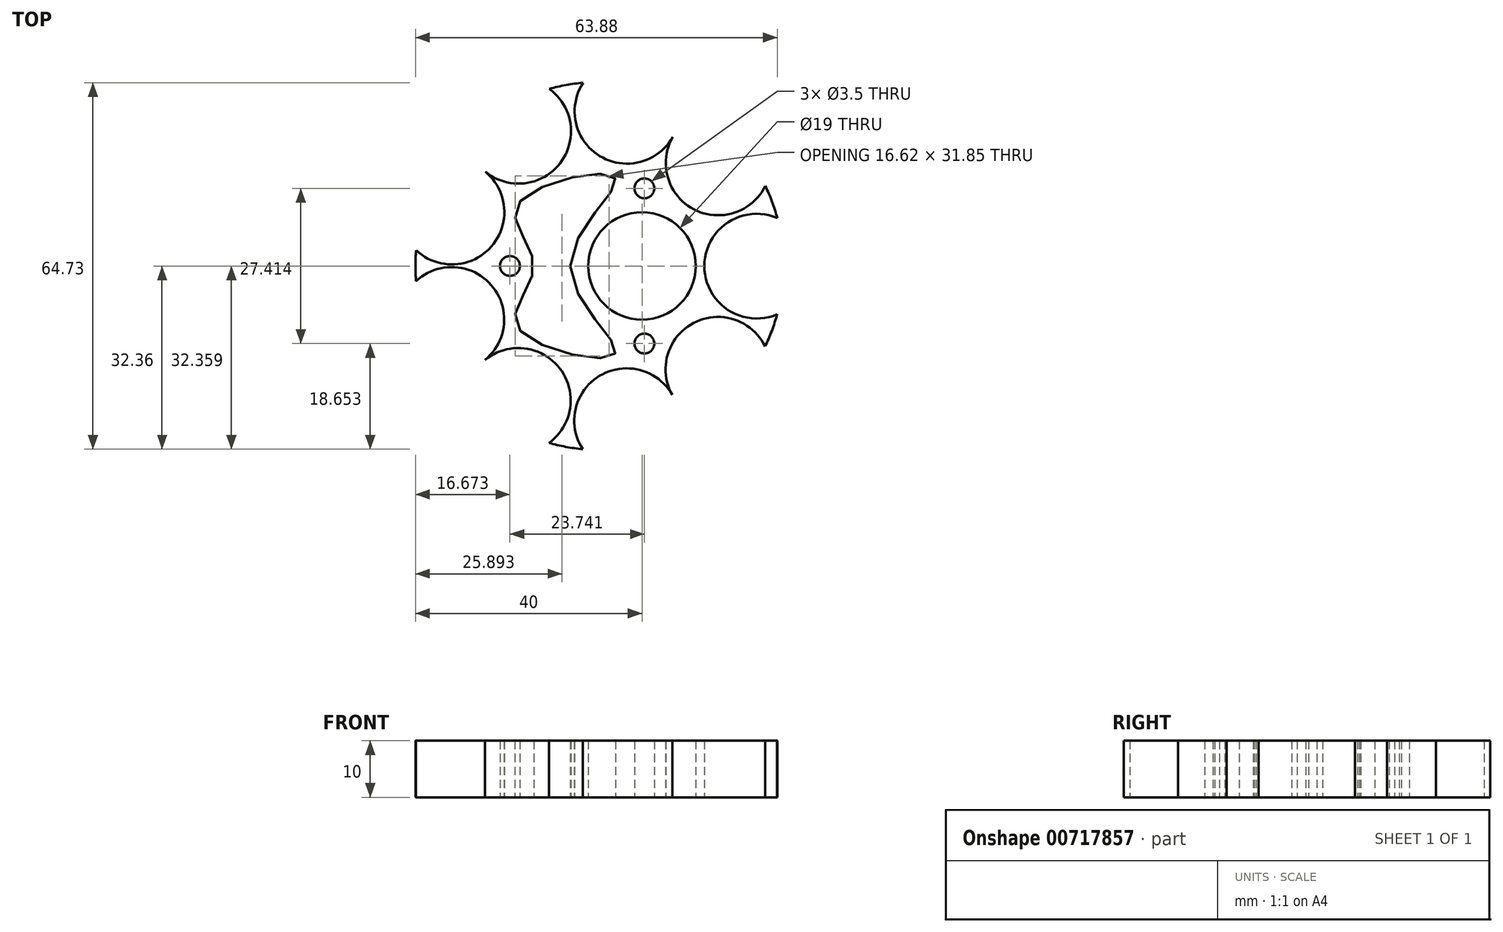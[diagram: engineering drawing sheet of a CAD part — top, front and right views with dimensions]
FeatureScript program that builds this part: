
annotation { "Feature Type Name" : "Feature", "Feature Type Description" : "" }
export const myFeature = defineFeature(function(context is Context, id is Id, definition is map)
    precondition{}
    {
        {
            var Q0;
            Q0=qCreatedBy(makeId("Top.planeOp"),FACE);
            var sketch = newSketch(context, id + "F0", { "sketchPlane" : qUnion([Q0])});
            skCircle(sketch, "E0", {"center": v(0, 0) * mm, "radius": 32.5 * mm});
            skCircle(sketch, "E1", {"center": v(27.75, -0.04) * mm, "radius": 9.25 * mm});
            skCircle(sketch, "E2.1.0", {"center": v(20.95, 18.2) * mm, "radius": 9.25 * mm});
            skCircle(sketch, "E2.2.0", {"center": v(4.85, 27.32) * mm, "radius": 9.25 * mm});
            skCircle(sketch, "E2.3.0", {"center": v(-14.29, 23.8) * mm, "radius": 9.25 * mm});
            skCircle(sketch, "E2.4.0", {"center": v(-26.06, 9.52) * mm, "radius": 9.25 * mm});
            skCircle(sketch, "E2.5.0", {"center": v(-26.09, -9.46) * mm, "radius": 9.25 * mm});
            skCircle(sketch, "E2.6.0", {"center": v(-14.35, -23.75) * mm, "radius": 9.25 * mm});
            skCircle(sketch, "E2.7.0", {"center": v(4.78, -27.33) * mm, "radius": 9.25 * mm});
            skCircle(sketch, "E2.8.0", {"center": v(20.9, -18.25) * mm, "radius": 9.25 * mm});
            skCircle(sketch, "E3", {"center": v(7.5, 0) * mm, "radius": 9.5 * mm});
            skCircle(sketch, "E4", {"center": v(-15.83, 0) * mm, "radius": 1.75 * mm});
            skCircle(sketch, "E5.1.0", {"center": v(7.91, -13.7) * mm, "radius": 1.75 * mm});
            skCircle(sketch, "E5.2.0", {"center": v(7.91, 13.7) * mm, "radius": 1.75 * mm});
            skPoint(sketch, "E6", {"position": v(2.64, 15.6) * mm});
            skPoint(sketch, "E7.MirrorP", {"position": v(2.64, -15.6) * mm});
            skPoint(sketch, "E8", {"position": v(-5.2, 0) * mm});
            skPoint(sketch, "E9", {"position": v(-11.6, 0) * mm});
            skPoint(sketch, "E10", {"position": v(-14.5, 10.8) * mm});
            skPoint(sketch, "E11.MirrorP", {"position": v(-14.5, -10.8) * mm});
            skFitSpline(sketch, "E12", {"points": [v(-5.2, 0) * mm, v(2.64, 15.6) * mm, v(-14.5, 10.8) * mm, v(-11.6, 0) * mm, v(-14.5, -10.8) * mm, v(2.64, -15.6) * mm, v(-5.2, 0) * mm]});
            skCircle(sketch, "E13", {"center": v(0, 0) * mm, "radius": 37 * mm, "construction": true});
            skSolve(sketch);
        }
        {
            var Q0;
            Q0=makeQuery(id+"F0.imprint","IMPRINT",FACE,{"disambiguationData":[TD([[makeQuery(id+"F0.imprint","IMPRINT",EDGE,{"derivedFrom":sQuery(id+"F0.wireOp",EDGE,"E4")}),-1.0]])]});
            extrude(context, id + "F1", {"entities" : qUnion([Q0]), "depth" : 10 * mm, "offsetDistance" : 25 * mm});
        }
    });
